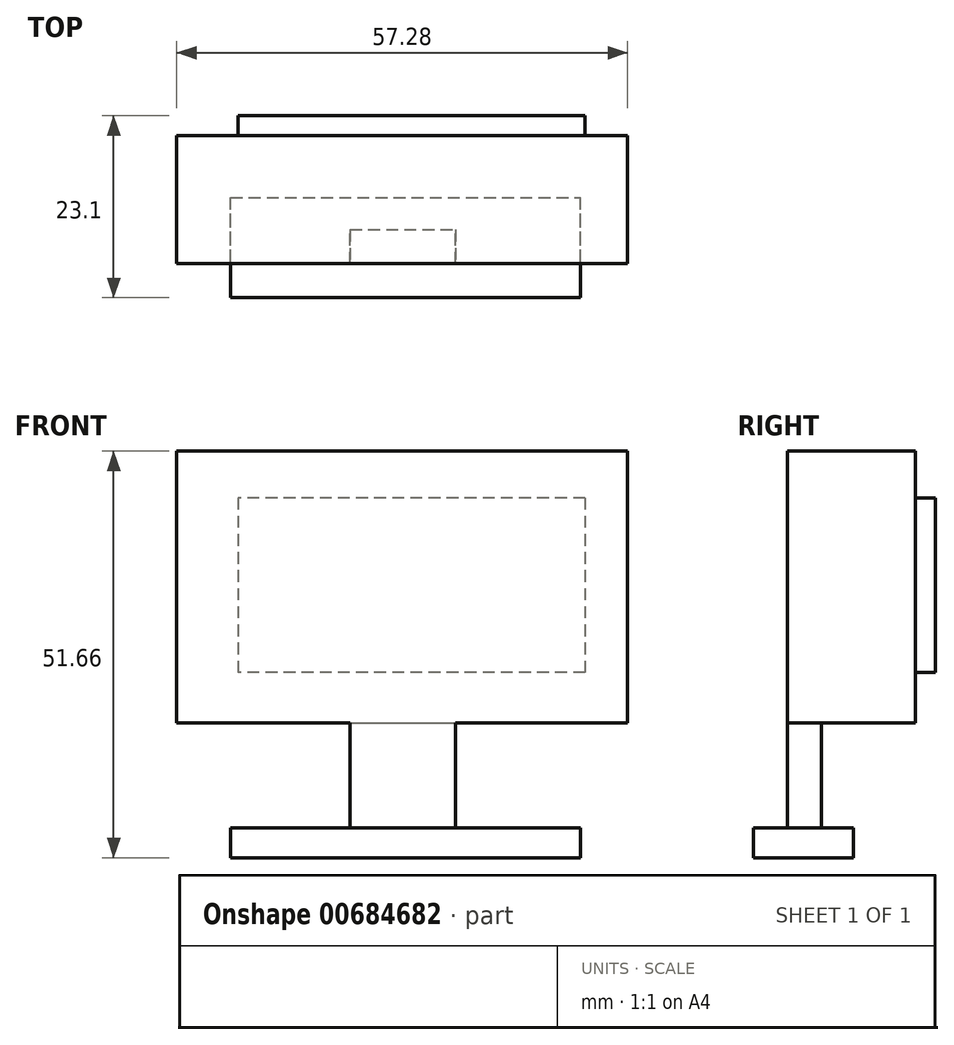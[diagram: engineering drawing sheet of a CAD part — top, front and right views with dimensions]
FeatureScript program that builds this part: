
annotation { "Feature Type Name" : "Feature", "Feature Type Description" : "" }
export const myFeature = defineFeature(function(context is Context, id is Id, definition is map)
    precondition{}
    {
        {
            var Q0;
            Q0=qCreatedBy(makeId("Top.planeOp"),FACE);
            var sketch = newSketch(context, id + "F0", { "sketchPlane" : qUnion([Q0])});
            skLineSegment(sketch, "E0.bottom", {"start": v(-15.17, -20.56) * mm, "end": v(29.28, -20.56) * mm});
            skLineSegment(sketch, "E0.top", {"start": v(-15.17, -7.86) * mm, "end": v(29.28, -7.86) * mm});
            skLineSegment(sketch, "E0.left", {"start": v(-15.17, -20.56) * mm, "end": v(-15.17, -7.86) * mm});
            skLineSegment(sketch, "E0.right", {"start": v(29.28, -20.56) * mm, "end": v(29.28, -7.86) * mm});
            skSolve(sketch);
        }
        {
            var Q0;
            Q0=qSketchRegion(id+"F0",true);
            extrude(context, id + "F1", {"entities" : qUnion([Q0]), "depth" : 3.8 * mm, "offsetDistance" : 25.4 * mm});
        }
        {
            var Q0;
            Q0=qCreatedBy(makeId("Top.planeOp"),FACE);
            var sketch = newSketch(context, id + "F2", { "sketchPlane" : qUnion([Q0])});
            skLineSegment(sketch, "E1.bottom", {"start": v(0, -11.94) * mm, "end": v(13.38, -11.94) * mm});
            skLineSegment(sketch, "E1.top", {"start": v(0, -16.26) * mm, "end": v(13.38, -16.26) * mm});
            skLineSegment(sketch, "E1.left", {"start": v(0, -11.94) * mm, "end": v(0, -16.26) * mm});
            skLineSegment(sketch, "E1.right", {"start": v(13.38, -11.94) * mm, "end": v(13.38, -16.26) * mm});
            skSolve(sketch);
        }
        {
            var Q0;
            Q0=qSketchRegion(id+"F2",true);
            extrude(context, id + "F3", {"entities" : qUnion([Q0]), "operationType" : NewBodyOperationType.ADD, "depth" : 50.8 * mm, "offsetDistance" : 25.4 * mm});
        }
        {
            var Q0;
            Q0=qCreatedBy(makeId("Front.planeOp"),FACE);
            var sketch = newSketch(context, id + "F4", { "sketchPlane" : qUnion([Q0])});
            skLineSegment(sketch, "E2.bottom", {"start": v(-22.02, 51.66) * mm, "end": v(35.26, 51.66) * mm});
            skLineSegment(sketch, "E2.top", {"start": v(-22.02, 17.12) * mm, "end": v(35.26, 17.12) * mm});
            skLineSegment(sketch, "E2.left", {"start": v(-22.02, 51.66) * mm, "end": v(-22.02, 17.12) * mm});
            skLineSegment(sketch, "E2.right", {"start": v(35.26, 51.66) * mm, "end": v(35.26, 17.12) * mm});
            skSolve(sketch);
        }
        {
            var Q0;
            Q0=qSketchRegion(id+"F4",true);
            extrude(context, id + "F5", {"entities" : qUnion([Q0]), "operationType" : NewBodyOperationType.ADD, "depth" : 16.26 * mm, "offsetDistance" : 25.4 * mm});
        }
        {
            var Q0;
            Q0=makeQuery(id+"F5.opExtrude","CAP_FACE",FACE,{"disambiguationData":[OSD([sQuery(id+"F4.wireOp",EDGE,"E2.bottom"),sQuery(id+"F4.wireOp",EDGE,"E2.top"),sQuery(id+"F4.wireOp",EDGE,"E2.left"),sQuery(id+"F4.wireOp",EDGE,"E2.right")])],"isStart":true});
            var sketch = newSketch(context, id + "F6", { "sketchPlane" : qUnion([Q0])});
            skLineSegment(sketch, "E3.bottom", {"start": v(-29.86, 45.73) * mm, "end": v(14.2, 45.73) * mm});
            skLineSegment(sketch, "E3.top", {"start": v(-29.86, 23.55) * mm, "end": v(14.2, 23.55) * mm});
            skLineSegment(sketch, "E3.left", {"start": v(-29.86, 45.73) * mm, "end": v(-29.86, 23.55) * mm});
            skLineSegment(sketch, "E3.right", {"start": v(14.2, 45.73) * mm, "end": v(14.2, 23.55) * mm});
            skSolve(sketch);
        }
        {
            var Q0;
            Q0=qSketchRegion(id+"F6",true);
            extrude(context, id + "F7", {"entities" : qUnion([Q0]), "operationType" : NewBodyOperationType.ADD, "depth" : 2.54 * mm, "offsetDistance" : 25.4 * mm});
        }
    });
